# Revit family: Wall_Hung _Multiple_Station_Hand_Wash_Sink-Elkay-EWMA72206
name_source: partatom
category: Plumbing Fixtures
units: mm (PartAtom-declared; Revit-internal decimal feet)

## family parameters
Cut with Voids When Loaded = No
Host = Face
Maintain Annotation Orientation = No
OmniClass Number = 23.45.05.14.14
OmniClass Title = Sinks/Lavatories
Part Type = Normal
Room Calculation Point = No
Round Connector Dimension = Use Diameter
Shared = No

## types (1)
- EWMA72206 (Wall Hung Multiple Station 6-Hole Sink)
    Approx. Shipping Weight (lbs) = 95
    Assembly Code = D2010400
    Back splash Height = 10.00"
    Back splash width = 2.00"
    Bowl  Dimensions = 69 inch x 16 1/2 inch x 8 inch
    Bowl Width = 16.50"
    Bowl length = 69.00"
    C/C distance of Center2-Hole pair = 8.00"
    CL of Hole = 3.50"
    Center 2-Hole pair = Yes
    Default Elevation = 48.00"
    Description = Stainless Steel 72 inch x 20 inch x 18 inch 6 Hole Wall Hung Multiple Station Hand Wash Sink
    Drain Location = Center
    Drain Location along x-axis = 34.50"
    Drain Location along y-axis = 6.88"
    Drain Size = 3.50"
    Front rim = 1.50"
    Guage = 14
    Installation type = Wall Hung
    Left side 2 Hole pair = Yes
    Main Material = Finish-Elkay-Stainless Steel
    Manufacturer = Elkay Manufacturer Company
    Manufacturer Brand = Elkay (by Zurn Elkay Water Solutions)
    Model = EWMA72206
    No of Bowls = 1
    Outlet Connection Size (inch) = 1.50"
    Product Documentation Link = https://www.elkayfiles.com
    Product Installation Sheet URL = https://www.elkayfiles.com
    Product Page URL = https://www.elkay.com
    Product Weight (lbs) = 93
    Product data URL = https://www.bimobject.com
    Repair Parts URL = https://www.elkayfiles.com
    Right side 2 Hole pair = Yes
    Rim = 1.50"
    Sink Depth = 18.00"
    Sink Dimensions = 72 inch x 20 inch x 18 inch
    Sink Length = 72.00"
    Sink Width = 20.00"
    URL = https://www.elkay.com
    center Hole = No

## geometry (parser evidence)
native form markers: Sweep x5
no freeform markers — native parametric forms only
